# Revit family: QF_Brema_G1000SPLIT_G1400SPLIT
name_source: partatom
category: Specialty Equipment
revit_build: Autodesk Revit 2014 (Build: 20130722_2115(x64)
units: mm (PartAtom-declared; Revit-internal decimal feet)

## types (2) — shared parameters
Apparent Power = 350 VA
Assembly Code = E1090320
BTUH = 0 W
Cold Water Connection Height = 140 mm
Cold Water Maximum Pressure = 6.0 bar
Cold Water Minimum Pressure = 1.0 bar
Cold Water Size = 1"
Cold Water Size Radius = 1/2"
Conn Conduit = Yes
Cycle = 50 Hz
Depth = 600 mm
Description = AUTOMATIC ICE CUBE MAKER AIR COOLED
Elec Conn Connection Height = 240 mm
FL Amps = 0 A
Height = 695 mm  [stored 2.28018 ft]
Indirect Waste Connection Height = 60 mm
Indirect Waste Radius = 1/2"
Indirect Waste Size = 1"
Manufacturer = BREMA
Max Overcurrent Protection = 0 A
Min Ckt Ampacity = 0 A
Model = G1000SPLIT
Phase = 1
URL = www.bremaice.it
Volts = 230 V
Watts = 350 W
Weight = 118 kg
Width = 765 mm  [stored 2.50984 ft]

## per-type parameters (varying)
| type | Refrigerant Type |
| G1000SPLIT | R404A |
| G1400SPLIT | CO2 |

note: [stored X ft] marks values corroborated as IEEE doubles in the binary element streams (Revit-internal decimal feet)

## geometry (parser evidence)
native form markers: Blend x7, Sweep x2
no freeform markers — native parametric forms only
